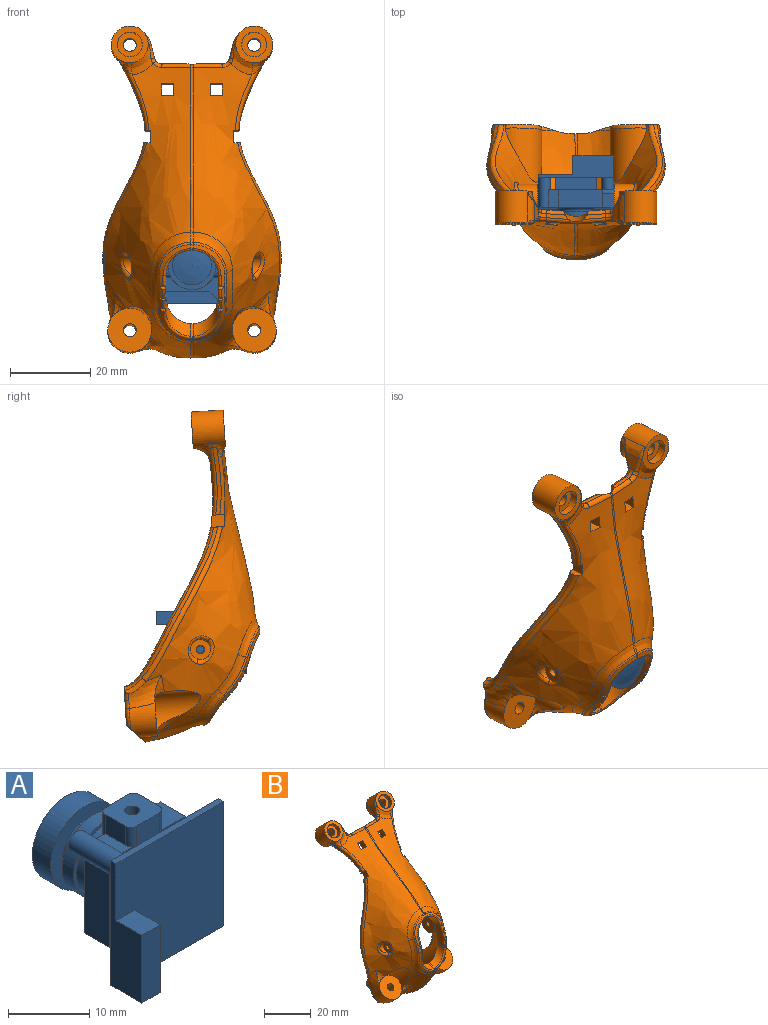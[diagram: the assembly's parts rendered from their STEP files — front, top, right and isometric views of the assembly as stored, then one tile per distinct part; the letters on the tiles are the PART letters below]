
ASSEMBLY  parts=2 mates=1
PART A: 64 faces, bbox 18.8x23x19 mm
  f0: plane 4.4x4.16mm, normal (0,0,-1), area 16mm2, adj f2,f4,f24,f46,f50
  f1: plane 4.4x2.04mm, normal (0,0,1), area 6.7mm2, adj f2,f4,f27,f55,f56
  f2: plane 16x6.4mm, normal (0,1,0), area 36.7mm2, adj f0,f1,f6,f24,f25,f26,f27,f44
  f3: plane 16x6.4mm, normal (0,1,0), area 36.7mm2, adj f7,f19,f20,f21,f22,f23,f28,f43
  f4: plane 15.56x6.52mm, normal (0,-1,0), area 33.6mm2, adj f0,f1,f24,f25,f26,f27,f30,f31
  f5: plane 15.56x6.52mm, normal (0,-1,0), area 33.6mm2, adj f19,f20,f21,f22,f23,f28,f29,f30
  f6: torus R=6mm, axis (0,1,0), area 17mm2, adj f2,f34,f44,f52
  f7: torus R=6mm, axis (0,1,0), area 17mm2, adj f3,f34,f43,f53
  f8: plane 1.5x1.5mm, normal (0,1,0), area 0.5mm2, adj f13,f14,f26
  f9: plane 18.8x18.8mm, normal (0,1,0), area 238.3mm2, adj f12,f13,f14,f15,f21,f26,f29,f30
  f10: plane 1.5x1.5mm, normal (0,1,0), area 0.5mm2, adj f12,f15,f21
  f11: plane 18.8x18.8mm, normal (0,-1,0), area 320.3mm2, adj f12,f13,f14,f15,f16,f17
  f12: plane 18.8x0.9mm, normal (1,0,0), area 16.9mm2, adj f9,f10,f11,f13,f15
  f13: plane 18.8x0.9mm, normal (0,0,1), area 16.9mm2, adj f8,f9,f11,f12,f14
  f14: plane 18.8x5.4mm, normal (-1,0,0), area 62.8mm2, adj f8,f9,f11,f13,f15,f16,f18
  f15: plane 18.8x5.4mm, normal (0,0,-1), area 31.5mm2, adj f9,f10,f11,f12,f14,f17,f18
  f16: plane 4.5x3.25mm, normal (0,0,1), area 14.6mm2, adj f11,f14,f17,f18
  f17: plane 10.2x4.5mm, normal (1,0,0), area 45.9mm2, adj f11,f15,f16,f18
  f18: plane 10.2x3.25mm, normal (0,-1,0), area 33.1mm2, adj f14,f15,f16,f17
  f19: plane 11.08x4.4mm, normal (1,0,0), area 48.7mm2, adj f3,f5,f20,f28
  f20: plane 4.4x2.36mm, normal (0.71,0,0.71), area 14.7mm2, adj f3,f5,f19,f21
  f21: cylinder r=1.5mm len=7.4mm, axis (0,-1,0), area 49mm2, adj f3,f5,f9,f10,f20,f22
  f22: plane 4.4x2.36mm, normal (-0.71,0,-0.71), area 14.7mm2, adj f3,f5,f21,f23
  f23: plane 4.4x2.04mm, normal (0,0,-1), area 6.7mm2, adj f3,f5,f22,f47,f49
  f24: plane 11.08x4.4mm, normal (-1,0,0), area 48.7mm2, adj f0,f2,f4,f25
  f25: plane 4.4x2.36mm, normal (-0.71,0,-0.71), area 14.7mm2, adj f2,f4,f24,f26
  f26: cylinder r=1.5mm len=7.4mm, axis (0,-1,0), area 49mm2, adj f2,f4,f8,f9,f25,f27
  f27: plane 4.4x2.36mm, normal (0.71,0,0.71), area 14.7mm2, adj f1,f2,f4,f26
  f28: plane 4.4x4.16mm, normal (0,0,1), area 16mm2, adj f3,f5,f19,f57,f58
  f29: plane 10x3mm, normal (1,0,0), area 30mm2, adj f5,f9,f30,f32
  f30: plane 10x3mm, normal (0,0,1), area 29.5mm2, adj f4,f5,f9,f29,f31,f51,f56,f57
  f31: plane 10x3mm, normal (-1,0,0), area 30mm2, adj f4,f9,f30,f32
  f32: plane 10x3mm, normal (0,0,-1), area 29.5mm2, adj f4,f5,f9,f29,f31,f46,f47,f48
  f33: plane 11x11mm, normal (0,-1,0), area 16.5mm2, adj f34,f41
  f34: cylinder r=5mm len=10mm, axis (0,-1,0), area 62.8mm2, adj f6,f7,f33,f45,f54
  f35: sphere r=23.77mm, area 74.7mm2, adj f36
  f36: plane 12x12mm, normal (0,1,0), area 39.2mm2, adj f35,f37
  f37: cylinder r=6mm len=12mm, axis (0,-1,0), area 120.6mm2, adj f36,f38
  f38: plane 12x12mm, normal (0,-1,0), area 65.3mm2, adj f37,f39
  f39: cylinder r=3.9mm len=7.8mm, axis (0,-1,0), area 36.8mm2, adj f38,f40
  f40: plane 11x11mm, normal (0,1,0), area 47.2mm2, adj f39,f41
  f41: cylinder r=5.5mm len=11mm, axis (0,-1,0), area 69.1mm2, adj f33,f40
  f42: plane 6x5.5mm, normal (0,0,-1), area 29.5mm2, adj f43,f44,f45,f46,f47,f48,f49,f50
  f43: cylinder r=1mm len=5.26mm, axis (0,0,-1), area 8mm2, adj f3,f7,f42,f45,f49
  f44: cylinder r=1mm len=5.26mm, axis (0,0,-1), area 8mm2, adj f2,f6,f42,f45,f50
  f45: plane 4.92x4mm, normal (0,1,0), area 18.5mm2, adj f34,f42,f43,f44
  f46: cylinder r=1mm len=4.5mm, axis (0,0,-1), area 5.3mm2, adj f0,f4,f32,f42,f48,f50
  f47: cylinder r=1mm len=4.5mm, axis (0,0,-1), area 5.3mm2, adj f5,f23,f32,f42,f48,f49
  f48: plane 4.5x4mm, normal (0,-1,0), area 18mm2, adj f32,f42,f46,f47
  f49: plane 3.5x2.9mm, normal (1,0,0), area 10.1mm2, adj f23,f42,f43,f47
  f50: plane 3.5x2.9mm, normal (-1,0,0), area 10.1mm2, adj f0,f42,f44,f46
  f51: plane 4.5x4mm, normal (0,-1,0), area 18mm2, adj f30,f56,f57,f59
  f52: cylinder r=1mm len=5.26mm, axis (0,0,-1), area 8mm2, adj f2,f6,f54,f55,f59
  f53: cylinder r=1mm len=5.26mm, axis (0,0,-1), area 8mm2, adj f3,f7,f54,f58,f59
  f54: plane 4.92x4mm, normal (0,1,0), area 18.5mm2, adj f34,f52,f53,f59
  f55: plane 3.5x2.9mm, normal (-1,0,0), area 10.1mm2, adj f1,f52,f56,f59
  f56: cylinder r=1mm len=4.5mm, axis (0,0,-1), area 5.3mm2, adj f1,f4,f30,f51,f55,f59
  f57: cylinder r=1mm len=4.5mm, axis (0,0,-1), area 5.3mm2, adj f5,f28,f30,f51,f58,f59
  f58: plane 3.5x2.9mm, normal (1,0,0), area 10.1mm2, adj f28,f53,f57,f59
  f59: plane 6x5.5mm, normal (0,0,1), area 29.5mm2, adj f51,f52,f53,f54,f55,f56,f57,f58
  f60: cylinder r=0.92mm len=3mm, axis (0,0,1), area 17.4mm2, adj f59,f61
  f61: plane 1.84x1.84mm, normal (0,0,1), area 2.7mm2, adj f60
  f62: cylinder r=0.92mm len=3mm, axis (0,0,-1), area 17.4mm2, adj f42,f63
  f63: plane 1.84x1.84mm, normal (0,0,-1), area 2.7mm2, adj f62
PART B: 207 faces, bbox 59.9x69.7x87.1 mm
  f0: offset ~83.38x64.32mm, area 1166.9mm2, adj f1,f179,f180,f181,f182,f183,f184,f185
  f1: plane 42.73x8.82mm, normal (0,0,-1), area 150.5mm2, adj f0,f2,f150,f151,f152,f153,f154,f155
  f2: offset ~83.38x64.32mm, area 1167mm2, adj f1,f3,f110,f111,f112,f113,f114,f115
  f3: cylinder r=6.5mm len=9.06mm, axis (0,0.94,0.34), area 37.8mm2, adj f2,f4,f109,f110
  f4: bspline ~9.45x7.43mm, area 9.7mm2, adj f3,f5,f104,f108
  f5: extruded ~0.61x0.5mm, area 0.4mm2, adj f4,f6,f103,f109
  f6: bspline ~9.45x7.43mm, area 9.7mm2, adj f5,f7,f102,f180
  f7: bspline ~10.3x1.54mm, area 3.8mm2, adj f6,f8,f99,f100,f101,f102,f181
  f8: plane 1.49x0.57mm, normal (0,-0.59,0.81), area 0.7mm2, adj f7,f9,f102
  f9: plane 1.49x0.57mm, normal (0,-0.81,-0.59), area 0.7mm2, adj f8,f10,f102,f181
  f10: bspline ~11.99x4.7mm, area 5.6mm2, adj f9,f11,f12,f98,f102,f181
  f11: plane 1.51x0.63mm, normal (0,-0.46,0.89), area 0.7mm2, adj f10,f98,f102
  f12: bspline ~8.27x7.22mm, area 9.9mm2, adj f10,f13,f102,f182
  f13: extruded ~0.76x0.5mm, area 0.4mm2, adj f12,f14,f15,f21
  f14: plane 3x1.73mm, normal (0,-0.5,-0.87), area 1.7mm2, adj f13,f111,f182,f183
  f15: bspline ~8.27x7.22mm, area 9.9mm2, adj f13,f16,f104,f111
  f16: bspline ~11.99x4.7mm, area 5.6mm2, adj f15,f17,f19,f20,f104,f110
  f17: plane 1.49x0.57mm, normal (0,-0.81,-0.59), area 0.7mm2, adj f16,f18,f104,f110
  f18: plane 1.49x0.57mm, normal (0,-0.59,0.81), area 0.7mm2, adj f17,f104,f108
  f19: plane 1.51x0.63mm, normal (0,-0.46,0.89), area 0.7mm2, adj f16,f20,f104
  f20: plane 1.67x0.79mm, normal (0,-0.89,-0.46), area 0.7mm2, adj f16,f19,f104
  f21: extruded ~0.72x0.64mm, area 0.5mm2, adj f13,f22,f102,f104
  f22: extruded ~0.53x0.5mm, area 0.3mm2, adj f21,f23,f36,f37
  f23: bspline ~9x8.93mm, area 8.2mm2, adj f22,f24,f35,f102
  f24: bspline ~12.77x3.71mm, area 7.4mm2, adj f23,f25,f34,f102
  f25: bspline ~13.31x4.39mm, area 27.1mm2, adj f24,f26,f35,f157
  f26: bspline ~12.1x10.04mm, area 39.7mm2, adj f25,f27,f34,f157
  f27: extruded ~2.12x1.67mm, area 1.4mm2, adj f26,f28,f33,f156
  f28: extruded ~0.5x0.5mm, area 0.3mm2, adj f27,f29,f34,f103
  f29: bspline ~9.63x8.97mm, area 8.6mm2, adj f28,f30,f33,f104
  f30: bspline ~12.77x3.71mm, area 7.4mm2, adj f29,f31,f36,f104
  f31: bspline ~12.73x4.11mm, area 27.1mm2, adj f30,f32,f33,f155
  f32: bspline ~10.71x10.27mm, area 38.5mm2, adj f31,f36,f37,f155
  f33: bspline ~12.1x10.04mm, area 39.7mm2, adj f27,f29,f31,f155
  f34: bspline ~9.63x8.97mm, area 8.4mm2, adj f24,f26,f28,f102
  f35: bspline ~10.71x10.27mm, area 38.5mm2, adj f23,f25,f37,f157
  f36: bspline ~8.35x8.01mm, area 8.2mm2, adj f22,f30,f32,f104
  f37: extruded ~2.41x1.29mm, area 1.4mm2, adj f22,f32,f35,f38
  f38: extruded ~32.91x25.65mm, area 20.9mm2, adj f37,f39,f155,f157
  f39: extruded ~0.98x0.5mm, area 0.5mm2, adj f38,f40,f69,f184
  f40: bspline ~10.47x1.89mm, area 11mm2, adj f39,f41,f68,f155,f184
  f41: bspline ~3.3x2.27mm, area 3.1mm2, adj f40,f42,f67,f155
  f42: bspline ~2.19x1.76mm, area 1.6mm2, adj f41,f43,f66,f67
  f43: bspline ~7.53x7.29mm, area 20.4mm2, adj f42,f44,f64,f65,f66,f155
  f44: plane 9.76x7.06mm, normal (0,-0.71,0.71), area 36.3mm2, adj f43,f45,f63,f64
  f45: cylinder r=4.6mm len=12.16mm, axis (0,-0.71,0.71), area 126.1mm2, adj f44,f46,f50,f51,f54,f55,f57,f65
  f46: bspline ~4.8x1.98mm, area 1.7mm2, adj f45,f47,f50,f114
  f47: bspline ~5.53x3.03mm, area 3.6mm2, adj f46,f48,f49,f114
  f48: plane 4.9x4.27mm, normal (0.97,0.17,0.17), area 10.7mm2, adj f47,f50,f66,f67
  f49: bspline ~2.17x2.01mm, area 2.4mm2, adj f47,f67,f113,f114
  f50: bspline ~12.24x12.21mm, area 18.4mm2, adj f45,f46,f48,f65
  f51: bspline ~3.69x2.64mm, area 2.7mm2, adj f45,f52,f54,f64
  f52: bspline ~14.88x14.31mm, area 22.8mm2, adj f51,f53,f64,f117,f155
  f53: bspline ~18.99x18.39mm, area 18.4mm2, adj f52,f54,f116,f117
  f54: bspline ~2.6x2.59mm, area 1.6mm2, adj f45,f51,f53,f55
  f55: bspline ~5.53x4.68mm, area 15.9mm2, adj f45,f54,f56,f116
  f56: bspline ~5.45x1.15mm, area 0.1mm2, adj f55,f57,f115,f116
  f57: plane 9.2x6.51mm, normal (0,0.71,-0.71), area 36.3mm2, adj f45,f56,f58,f115
  f58: cone r=3.1mm half-angle=45deg, axis (0,0.71,-0.71), area 12.7mm2, adj f57,f59
  f59: cylinder r=2.6mm len=5.44mm, axis (0,-0.71,0.71), area 40.8mm2, adj f58,f60
  f60: plane 5.2x3.68mm, normal (0,0.71,-0.71), area 13.2mm2, adj f59,f61
  f61: cylinder r=1.6mm len=4.38mm, axis (0,0.71,-0.71), area 30.2mm2, adj f60,f62
  f62: plane 6.2x4.38mm, normal (0,-0.71,0.71), area 22.1mm2, adj f61,f63
  f63: cylinder r=3.1mm len=6.2mm, axis (0,0.71,-0.71), area 39mm2, adj f44,f62
  f64: bspline ~3.57x3.48mm, area 6.6mm2, adj f43,f44,f51,f52
  f65: bspline ~3.55x2.96mm, area 2.2mm2, adj f43,f45,f50,f66
  f66: bspline ~5.31x4.18mm, area 4.5mm2, adj f42,f43,f48,f65
  f67: cylinder r=2mm len=2.27mm, axis (0,0.71,-0.71), area 3.1mm2, adj f41,f42,f48,f49,f68,f113
  f68: plane 5.67x1.03mm, normal (0,0.71,0.71), area 5.1mm2, adj f40,f67,f112,f184
  f69: bspline ~10.47x1.89mm, area 11mm2, adj f39,f70,f97,f157,f184
  f70: bspline ~3.3x2.27mm, area 3.1mm2, adj f69,f71,f96,f157
  f71: cylinder r=2mm len=2.27mm, axis (0,0.71,-0.71), area 3.1mm2, adj f70,f72,f95,f96,f97,f186
  f72: plane 4.9x4.27mm, normal (-0.97,0.17,0.17), area 10.7mm2, adj f71,f73,f93,f94
  f73: bspline ~5.53x3.03mm, area 3.6mm2, adj f72,f74,f95,f187
  f74: bspline ~4.8x1.98mm, area 1.7mm2, adj f73,f75,f93,f187
  f75: cylinder r=4.6mm len=12.16mm, axis (0,-0.71,0.71), area 126.1mm2, adj f74,f76,f84,f85,f90,f91,f92,f93
  f76: plane 9.2x6.51mm, normal (0,0.71,-0.71), area 36.3mm2, adj f75,f77,f78,f188
  f77: bspline ~5.45x1.15mm, area 0.1mm2, adj f76,f84,f188,f189
  f78: cone r=3.1mm half-angle=45deg, axis (0,0.71,-0.71), area 12.7mm2, adj f76,f79
  f79: cylinder r=2.6mm len=5.44mm, axis (0,-0.71,0.71), area 40.8mm2, adj f78,f80
  f80: plane 5.2x3.68mm, normal (0,0.71,-0.71), area 13.2mm2, adj f79,f81
  f81: cylinder r=1.6mm len=4.38mm, axis (0,0.71,-0.71), area 30.2mm2, adj f80,f82
  f82: plane 6.2x4.38mm, normal (0,-0.71,0.71), area 22.1mm2, adj f81,f83
  f83: cylinder r=3.1mm len=6.2mm, axis (0,0.71,-0.71), area 39mm2, adj f82,f91
  f84: bspline ~5.52x5mm, area 16.5mm2, adj f75,f77,f85,f189
  f85: bspline ~2.6x2.59mm, area 1.6mm2, adj f75,f84,f86,f90
  f86: bspline ~18.99x18.39mm, area 18.4mm2, adj f85,f87,f189,f190
  f87: bspline ~14.88x14.31mm, area 22.8mm2, adj f86,f88,f90,f157,f190
  f88: bspline ~3.57x3.48mm, area 6.6mm2, adj f87,f89,f90,f91
  f89: bspline ~7.53x7.29mm, area 20.4mm2, adj f88,f91,f92,f94,f96,f157
  f90: bspline ~3.09x2.06mm, area 2.7mm2, adj f75,f85,f87,f88
  f91: plane 9.76x7.06mm, normal (0,-0.71,0.71), area 36.3mm2, adj f75,f83,f88,f89
  f92: bspline ~3.55x2.96mm, area 2.2mm2, adj f75,f89,f93,f94
  f93: bspline ~12.24x12.21mm, area 18.4mm2, adj f72,f74,f75,f92
  f94: bspline ~5.31x4.18mm, area 4.5mm2, adj f72,f89,f92,f96
  f95: bspline ~2.17x2.01mm, area 2.4mm2, adj f71,f73,f186,f187
  f96: bspline ~2.19x1.76mm, area 1.6mm2, adj f70,f71,f89,f94
  f97: plane 5.67x1.03mm, normal (0,0.71,0.71), area 5.1mm2, adj f69,f71,f184,f185
  f98: plane 1.67x0.79mm, normal (0,-0.89,-0.46), area 0.7mm2, adj f10,f11,f102
  f99: plane 1.63x0.66mm, normal (0,-0.71,-0.71), area 0.7mm2, adj f7,f100,f101,f102
  f100: extruded ~0.99x0.02mm, area 0mm2, adj f7,f99,f101
  f101: plane 1.63x0.66mm, normal (0,-0.71,0.71), area 0.7mm2, adj f7,f99,f100,f102
  f102: offset ~73.93x54.26mm, area 38.2mm2, adj f6,f7,f8,f9,f10,f11,f12,f21
  f103: extruded ~0.72x0.5mm, area 0.4mm2, adj f5,f28,f102,f104
  f104: offset ~73.93x54.26mm, area 38.2mm2, adj f4,f15,f16,f17,f18,f19,f20,f21
  f105: plane 1.63x0.66mm, normal (0,-0.71,0.71), area 0.7mm2, adj f104,f106,f107,f108
  f106: extruded ~0.99x0.02mm, area 0mm2, adj f105,f107,f108
  f107: plane 1.63x0.66mm, normal (0,-0.71,-0.71), area 0.7mm2, adj f104,f105,f106,f108
  f108: bspline ~10.3x1.54mm, area 3.8mm2, adj f4,f18,f104,f105,f106,f107,f110
  f109: plane 3.33x1.21mm, normal (0,-0.34,0.94), area 1.8mm2, adj f3,f5,f179,f180
  f110: plane 10.55x5.43mm, normal (1,0,0), area 34.9mm2, adj f2,f3,f16,f17,f108,f111
  f111: cylinder r=6.5mm len=8.13mm, axis (0,0.87,-0.5), area 36mm2, adj f2,f14,f15,f110
  f112: bspline ~7.44x1.8mm, area 7.2mm2, adj f2,f68,f113,f184
  f113: bspline ~2.84x1.75mm, area 2.1mm2, adj f2,f49,f67,f112
  f114: bspline ~11.02x10.53mm, area 30.6mm2, adj f2,f45,f46,f47,f49,f115
  f115: bspline ~6.13x4.96mm, area 14.6mm2, adj f2,f56,f57,f114
  f116: bspline ~15.96x15.64mm, area 28.1mm2, adj f2,f53,f55,f56,f117
  f117: plane 2.27x2.27mm, normal (0,-0.71,-0.71), area 3.5mm2, adj f2,f52,f53,f116,f119,f155
  f118: bspline ~3.81x2.88mm, area 0mm2, adj f2,f119
  f119: plane 4.78x4.2mm, normal (-1,0,0), area 9.6mm2, adj f2,f117,f118,f120,f155
  f120: plane 2.6x2.6mm, normal (0,0.71,0.71), area 4.4mm2, adj f2,f119,f121,f131,f132,f155
  f121: bspline ~44.48x12.97mm, area 63.5mm2, adj f120,f122,f131,f155
  f122: bspline ~7.25x2.84mm, area 7.9mm2, adj f121,f123,f130,f131,f151
  f123: bspline ~13.39x11.03mm, area 39.6mm2, adj f122,f124,f128,f129,f130,f153,f155
  f124: plane 11.03x7.81mm, normal (0,-0.71,0.71), area 87.1mm2, adj f123,f125,f127,f128,f153
  f125: cylinder r=5.5mm len=15.27mm, axis (0,0.71,-0.71), area 101.2mm2, adj f124,f126,f128,f154,f155
  f126: bspline ~7.27x6.73mm, area 11.1mm2, adj f125,f154,f155
  f127: cylinder r=1.6mm len=7.53mm, axis (0,0.71,-0.71), area 74.9mm2, adj f124,f151
  f128: bspline ~7.81x7.65mm, area 10.8mm2, adj f123,f124,f125,f155
  f129: bspline ~3.81x3.61mm, area 2.7mm2, adj f123,f130,f151,f152
  f130: bspline ~3.59x3.34mm, area 2.7mm2, adj f122,f123,f129,f151
  f131: bspline ~48.07x13.97mm, area 50.4mm2, adj f120,f121,f122,f132,f151
  f132: bspline ~45.48x12.06mm, area 81mm2, adj f2,f120,f131,f151
  f133: cylinder r=7mm len=15.45mm, axis (0,0.71,-0.71), area 131.2mm2, adj f2,f134
  f134: torus R=6mm, axis (0,-0.71,0.71), area 17.9mm2, adj f2,f133,f150,f151
  f135: bspline ~6.77x3.33mm, area 11.7mm2, adj f2,f136,f143
  f136: plane 8.09x8.09mm, normal (1,0,0), area 46.8mm2, adj f135,f137,f138
  f137: cylinder r=4mm len=8mm, axis (1,0,0), area 56.2mm2, adj f136,f143
  f138: cylinder r=1.05mm len=5.5mm, axis (-1,0,0), area 36.3mm2, adj f136,f139
  f139: plane 5.39x5.39mm, normal (-1,0,0), area 16.2mm2, adj f138,f140,f142
  f140: cylinder r=2.5mm len=4.98mm, axis (-1,0,0), area 0mm2, adj f139,f141
  f141: bspline ~7.14x4.82mm, area 14.7mm2, adj f140,f142,f155
  f142: bspline ~6.99x3.93mm, area 8.9mm2, adj f139,f141,f155
  f143: bspline ~10.31x9.98mm, area 37.2mm2, adj f2,f135,f137
  f144: plane 3.14x2.42mm, normal (0,0.71,0.71), area 9mm2, adj f2,f145,f147,f155
  f145: plane 4.32x4.22mm, normal (1,0,0), area 9mm2, adj f2,f144,f146,f155
  f146: plane 3.17x2.43mm, normal (0,-0.71,-0.71), area 9mm2, adj f2,f145,f147,f155
  f147: plane 4.36x4.22mm, normal (-1,0,0), area 9mm2, adj f2,f144,f146,f155
  f148: plane 5.99x5.14mm, normal (1,0,0), area 14.4mm2, adj f2,f149
  f149: cylinder r=3.5mm len=5.99mm, axis (1,0,0), area 0mm2, adj f2,f148
  f150: bspline ~6.18x3.51mm, area 2.8mm2, adj f1,f2,f134,f151
  f151: plane 11.84x6.92mm, normal (0,0.71,-0.71), area 78.6mm2, adj f1,f2,f122,f127,f129,f130,f131,f132
  f152: torus R=4.5mm, axis (0,-0.71,0.71), area 5.8mm2, adj f1,f129,f151,f153
  f153: cylinder r=5.5mm len=10.45mm, axis (0,0.71,-0.71), area 82.9mm2, adj f1,f123,f124,f152,f154
  f154: bspline ~10.34x9.11mm, area 31.9mm2, adj f1,f125,f126,f153,f155
  f155: bspline ~77.07x58.32mm, area 1188.6mm2, adj f1,f31,f32,f33,f38,f40,f41,f43
  f156: extruded ~10.63x6.39mm, area 6.2mm2, adj f1,f27,f155,f157
  f157: bspline ~77.07x58.32mm, area 1188.6mm2, adj f1,f25,f26,f35,f38,f69,f70,f87
  f158: bspline ~43.59x12.97mm, area 63.5mm2, adj f157,f159,f160,f193
  f159: bspline ~48.07x13.97mm, area 50.4mm2, adj f158,f160,f193,f194,f195
  f160: bspline ~7.25x2.84mm, area 7.9mm2, adj f158,f159,f161,f163,f195
  f161: bspline ~3.59x3.34mm, area 2.7mm2, adj f160,f162,f163,f195
  f162: bspline ~3.81x3.61mm, area 2.7mm2, adj f161,f163,f178,f195
  f163: bspline ~13.07x10.82mm, area 39.6mm2, adj f157,f160,f161,f162,f164,f166,f177
  f164: plane 11.03x7.81mm, normal (0,-0.71,0.71), area 87.1mm2, adj f163,f165,f166,f167,f177
  f165: cylinder r=1.6mm len=7.53mm, axis (0,0.71,-0.71), area 74.9mm2, adj f164,f195
  f166: bspline ~7.81x7.65mm, area 10.8mm2, adj f157,f163,f164,f167
  f167: cylinder r=5.5mm len=15.27mm, axis (0,0.71,-0.71), area 101.2mm2, adj f157,f164,f166,f168,f176
  f168: bspline ~7.27x6.73mm, area 11.1mm2, adj f157,f167,f176
  f169: bspline ~7.14x4.82mm, area 14.7mm2, adj f157,f170,f175
  f170: cylinder r=2.5mm len=4.98mm, axis (1,0,0), area 0mm2, adj f169,f171
  f171: plane 5.39x5.39mm, normal (1,0,0), area 16.2mm2, adj f170,f172,f175
  f172: cylinder r=1.05mm len=5.5mm, axis (1,0,0), area 36.3mm2, adj f171,f173
  f173: plane 8.09x8.09mm, normal (-1,0,0), area 46.8mm2, adj f172,f174,f200
  f174: cylinder r=4mm len=8mm, axis (-1,0,0), area 56.2mm2, adj f173,f199
  f175: bspline ~6.99x3.93mm, area 8.9mm2, adj f157,f169,f171
  f176: bspline ~10.34x9.11mm, area 31.9mm2, adj f1,f157,f167,f168,f177
  f177: cylinder r=5.5mm len=10.45mm, axis (0,0.71,-0.71), area 82.9mm2, adj f1,f163,f164,f176,f178
  f178: torus R=4.5mm, axis (0,-0.71,0.71), area 5.8mm2, adj f1,f162,f177,f195
  f179: extruded ~15.8x8.98mm, area 9.1mm2, adj f0,f1,f2,f109
  f180: cylinder r=6.5mm len=9.06mm, axis (0,0.94,0.34), area 37.8mm2, adj f0,f6,f109,f181
  f181: plane 10.55x5.43mm, normal (-1,0,0), area 34.9mm2, adj f0,f7,f9,f10,f180,f182
  f182: cylinder r=6.5mm len=8.13mm, axis (0,0.87,-0.5), area 36mm2, adj f0,f12,f14,f181
  f183: extruded ~27.76x21.32mm, area 17.5mm2, adj f0,f2,f14,f184
  f184: cylinder r=3mm len=10.86mm, axis (0,0.57,0.82), area 70mm2, adj f0,f2,f39,f40,f68,f69,f97,f112
  f185: bspline ~7.44x1.8mm, area 7.2mm2, adj f0,f97,f184,f186
  f186: bspline ~2.84x1.75mm, area 2.1mm2, adj f0,f71,f95,f185
  f187: bspline ~10.96x10.5mm, area 30.6mm2, adj f0,f73,f74,f75,f95,f188
  f188: bspline ~6.13x4.96mm, area 14.6mm2, adj f0,f76,f77,f187
  f189: bspline ~14.59x14.53mm, area 28.1mm2, adj f0,f77,f84,f86,f190
  f190: plane 2.27x2.27mm, normal (0,-0.71,-0.71), area 3.5mm2, adj f0,f86,f87,f157,f189,f192
  f191: bspline ~3.81x2.88mm, area 0mm2, adj f0,f192
  f192: plane 4.78x4.2mm, normal (1,0,0), area 9.6mm2, adj f0,f157,f190,f191,f193
  f193: plane 2.6x2.6mm, normal (0,0.71,0.71), area 4.4mm2, adj f0,f157,f158,f159,f192,f194
  f194: bspline ~45.48x12.06mm, area 81mm2, adj f0,f159,f193,f195
  f195: plane 11.84x6.92mm, normal (0,0.71,-0.71), area 78.6mm2, adj f0,f1,f159,f160,f161,f162,f165,f178
  f196: cylinder r=7mm len=15.45mm, axis (0,0.71,-0.71), area 131.3mm2, adj f0,f197
  f197: torus R=6mm, axis (0,-0.71,0.71), area 17.9mm2, adj f0,f195,f196,f198
  f198: bspline ~6.18x3.51mm, area 2.8mm2, adj f0,f1,f195,f197
  f199: bspline ~10.31x9.72mm, area 37.2mm2, adj f0,f174,f200
  f200: bspline ~6.77x3.33mm, area 11.7mm2, adj f0,f173,f199
  f201: plane 4.36x4.22mm, normal (1,0,0), area 9mm2, adj f0,f157,f202,f204
  f202: plane 3.14x2.42mm, normal (0,0.71,0.71), area 9mm2, adj f0,f157,f201,f203
  f203: plane 4.32x4.22mm, normal (-1,0,0), area 9mm2, adj f0,f157,f202,f204
  f204: plane 3.17x2.43mm, normal (0,-0.71,-0.71), area 9mm2, adj f0,f157,f201,f203
  f205: cylinder r=3.5mm len=5.99mm, axis (-1,0,0), area 0mm2, adj f0,f206
  f206: plane 5.99x5.14mm, normal (-1,0,0), area 14.4mm2, adj f0,f205
PLACE A rot(axis=(0.71,0,-0.71),180deg) t=(0,-7,9.4)mm
PLACE B rot(axis=(1,0,0),41.4deg) t=(0,-5.11,-15.49)mm
MATE revolute A.f60 <-> B.f137  axis (1,0,0) through (9.5,-6.55,9.4)mm
